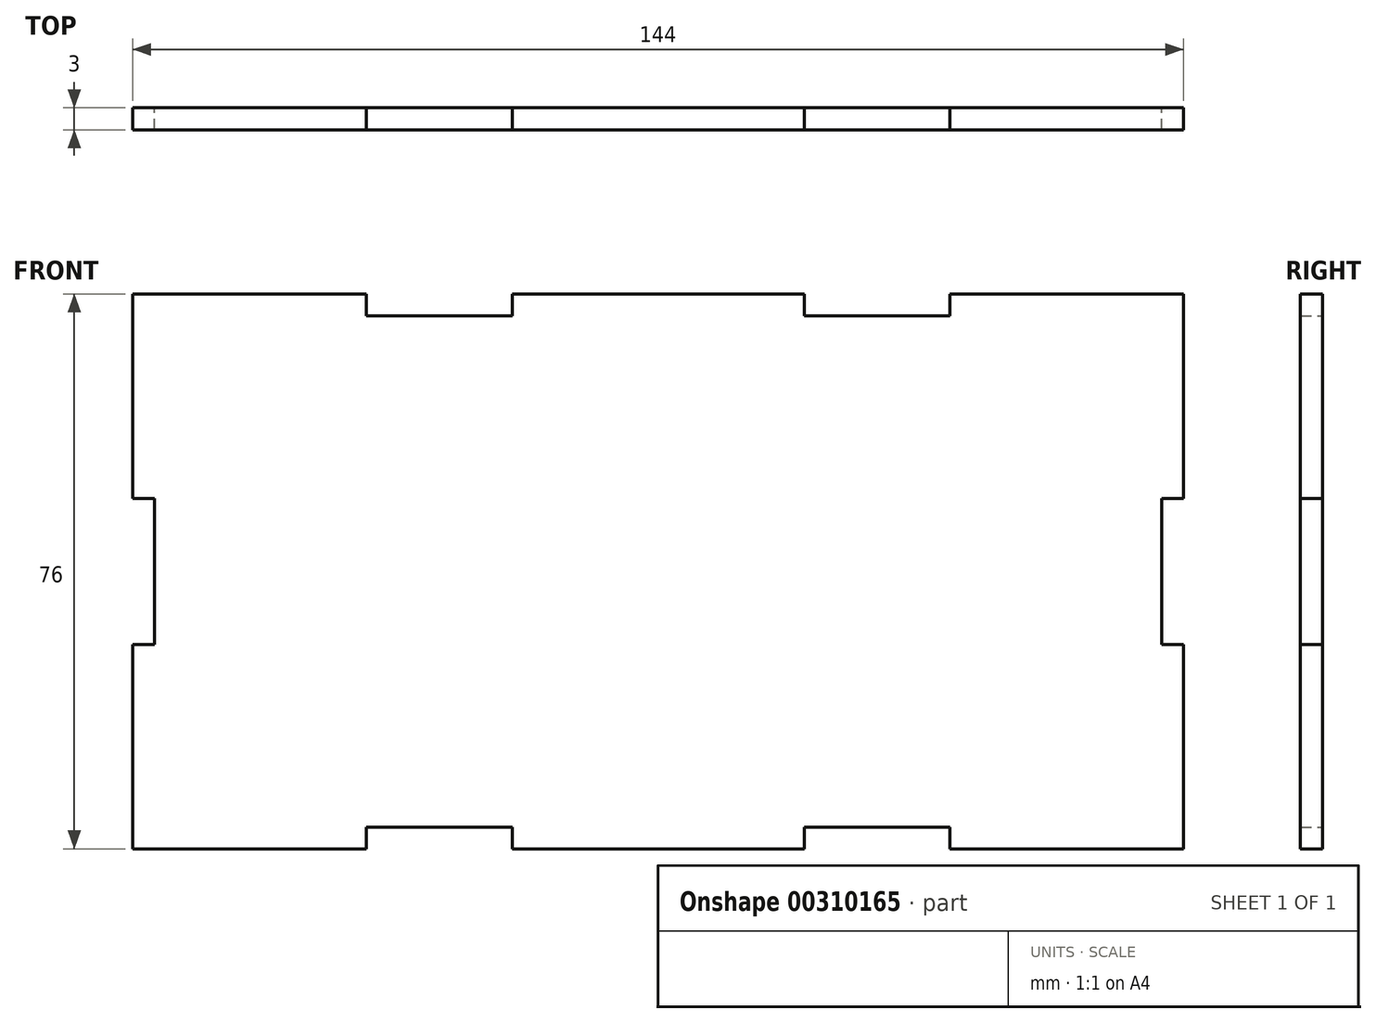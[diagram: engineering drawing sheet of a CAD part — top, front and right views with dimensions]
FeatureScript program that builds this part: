
annotation { "Feature Type Name" : "Feature", "Feature Type Description" : "" }
export const myFeature = defineFeature(function(context is Context, id is Id, definition is map)
    precondition{}
    {
        {
            var Q0;
            Q0=qCreatedBy(makeId("Front.planeOp"),FACE);
            var sketch = newSketch(context, id + "F0", { "sketchPlane" : qUnion([Q0])});
            skLineSegment(sketch, "E0.bottom", {"start": v(72, -38) * mm, "end": v(40, -38) * mm});
            skLineSegment(sketch, "E0.top", {"start": v(72, 38) * mm, "end": v(40, 38) * mm});
            skLineSegment(sketch, "E0.left", {"start": v(72, -38) * mm, "end": v(72, -10) * mm});
            skLineSegment(sketch, "E0.right", {"start": v(-72, -38) * mm, "end": v(-72, -10) * mm});
            skPoint(sketch, "E0.middle", {"position": v(0, 0) * mm});
            skLineSegment(sketch, "E1.bottom", {"start": v(-72, 10) * mm, "end": v(-69, 10) * mm});
            skLineSegment(sketch, "E1.top", {"start": v(-72, -10) * mm, "end": v(-69, -10) * mm});
            skLineSegment(sketch, "E1.right", {"start": v(-69, 10) * mm, "end": v(-69, -10) * mm});
            skLineSegment(sketch, "E2.top", {"start": v(-20, 35) * mm, "end": v(-40, 35) * mm});
            skLineSegment(sketch, "E2.left", {"start": v(-20, 38) * mm, "end": v(-20, 35) * mm});
            skLineSegment(sketch, "E2.right", {"start": v(-40, 38) * mm, "end": v(-40, 35) * mm});
            skLineSegment(sketch, "E3.MirrorCS", {"start": v(40, 38) * mm, "end": v(40, 35) * mm});
            skLineSegment(sketch, "E4.MirrorCS", {"start": v(20, 38) * mm, "end": v(20, 35) * mm});
            skLineSegment(sketch, "E5.MirrorCS", {"start": v(20, 35) * mm, "end": v(40, 35) * mm});
            skLineSegment(sketch, "E6.MirrorCS", {"start": v(69, 10) * mm, "end": v(69, -10) * mm});
            skLineSegment(sketch, "E7.MirrorCS", {"start": v(72, -10) * mm, "end": v(69, -10) * mm});
            skLineSegment(sketch, "E8.MirrorCS", {"start": v(72, 10) * mm, "end": v(69, 10) * mm});
            skLineSegment(sketch, "E9.MirrorCS", {"start": v(-40, -38) * mm, "end": v(-40, -35) * mm});
            skLineSegment(sketch, "E10.MirrorCS", {"start": v(-20, -38) * mm, "end": v(-20, -35) * mm});
            skLineSegment(sketch, "E11.MirrorCS", {"start": v(-20, -35) * mm, "end": v(-40, -35) * mm});
            skLineSegment(sketch, "E12.MirrorCS", {"start": v(40, -38) * mm, "end": v(40, -35) * mm});
            skLineSegment(sketch, "E13.MirrorCS", {"start": v(20, -38) * mm, "end": v(20, -35) * mm});
            skLineSegment(sketch, "E14.MirrorCS", {"start": v(20, -35) * mm, "end": v(40, -35) * mm});
            skLineSegment(sketch, "E15.trimOffspring", {"start": v(-40, 38) * mm, "end": v(-72, 38) * mm});
            skLineSegment(sketch, "E16.trimOffspring", {"start": v(-72, 10) * mm, "end": v(-72, 38) * mm});
            skLineSegment(sketch, "E17.trimOffspring", {"start": v(-40, -38) * mm, "end": v(-72, -38) * mm});
            skLineSegment(sketch, "E18.trimOffspring", {"start": v(20, -38) * mm, "end": v(-20, -38) * mm});
            skLineSegment(sketch, "E19.trimOffspring", {"start": v(20, 38) * mm, "end": v(-20, 38) * mm});
            skLineSegment(sketch, "E20.trimOffspring", {"start": v(72, 10) * mm, "end": v(72, 38) * mm});
            skSolve(sketch);
        }
        {
            var Q0;
            Q0 = qSketchRegion(id + "F0", true);
            extrude(context, id + "F1", {"entities" : qUnion([Q0]), "depth" : 3 * mm});
        }
    });
